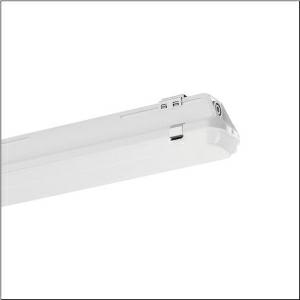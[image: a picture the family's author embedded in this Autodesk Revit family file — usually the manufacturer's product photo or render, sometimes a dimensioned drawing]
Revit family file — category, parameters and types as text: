
# Revit family: monsun_21_51fb207p660c005
name_source: partatom
category: Lighting Fixtures
units: mm (PartAtom-declared; Revit-internal decimal feet)

## family parameters
Cut with Voids When Loaded = No
Host = Face
Light Source = No
Part Type = Normal
Room Calculation Point = No
Round Connector Dimension = Use Diameter
Shared = No

## types (1)
- Monsun 21 (1 x LED, 5410 lm, 34.9 W, 6500K)
    Apparent Load = 35 VA
    CIE Flux Codes = 45 75 93 94 100
    Color Rendering = 80
    Color Temperature = 6500K
    Default Elevation = 1800 mm
    Description = Monsun 21, damp-proof luminaire, chain hanger, primary optical cover: enclosure, of PC, light emission: direct distribution, primary light characteristic: symmetric, installation type: suspended mounting, surface-mounted, horizontal mounting, vertical mounting, LED, rated luminous flux: 5.410lm, luminous efficacy: 155lm/W, light colour: 865, colour temperature: 6500K, control gear: ON/OFF, with terminal, 3-pole, max. 2.5mm², through-wiring: 5x 2.5mm², mains connection: 220..240V, AC, 50/60Hz, rated input power: 35W, housing, of glass-fibre reinforced polyester, uncoated, bright grey, incl. chain hanger, length: 1.590mm, width: 90mm, height: 88mm, clip for enclosure, of stainless steel (V2A), ceiling mounting element, of stainless steel (V2A), chain hanger, of stainless steel (V2A), protection rating (complete): IP66, insulation class (complete): insulation class I (protective earthing), certification: CE, ENEC, VDE, UKCA, protection symbol: D, impact resistance: IK08, permissible operating ambient temperature: -25..+35°C, standard: EN 50419, EN 60598-2-1, corresponds to IFS (International Featured Standards) requirements for safety and quality in the food industry, for indoor or canopied outdoor use, no direct snow, no direct sun, no direct rain, LABS conformity tested according to VDMA 24364:2018-05, contact your sales advisor before using the luminaires in applications with unclear chemical exposure, large temperature fluctuations or condensation-forming humidity, packaging unit: 1 piece
    Height = 89 mm
    Lamp = 1 x LED
    Lamp Light Flux = 5410 lm
    Lamp Power = 34.9 W
    Lamp count = 1
    Length = 1590 mm
    Luminous efficacy = 155 lm/W
    Manufacturer = Siteco
    ModVariant = No
    Model = 51FB207P660C005
    Mounting Place = Ceiling
    Mounting Type = Surface mounted
    Number of Poles = 1
    OnlyDefault = Yes
    Power Factor = 1
    Product Name = Monsun 21
    Product group = damp-proof luminaire
    ProductGroupID = 300
    Protection Class = Protection class I
    Protection Degree = IP 66
    RLX_Detail_Level = 1
    RLX_Emergency_Light_Flux = 0 lm
    RLX_Emergency_Type = 0
    RLX_Emergency_Type_DB = No
    RlxData = <blob elided: 88677 chars, md5=855d88d4>
    Socket = socket
    Standby Power = 0 W
    System Light Flux = 5410 lm
    System Power = 35 W
    Type Comments = Product without accessories
    Type Image = l_1319656.jpg
    URL = http://relux.com
    VarID = ---
    Voltage = 0 V
    Weight = 0.00 kg
    Width = 90 mm

## geometry (parser evidence)
native form markers: Blend x4, Sweep x15
no freeform markers — native parametric forms only
